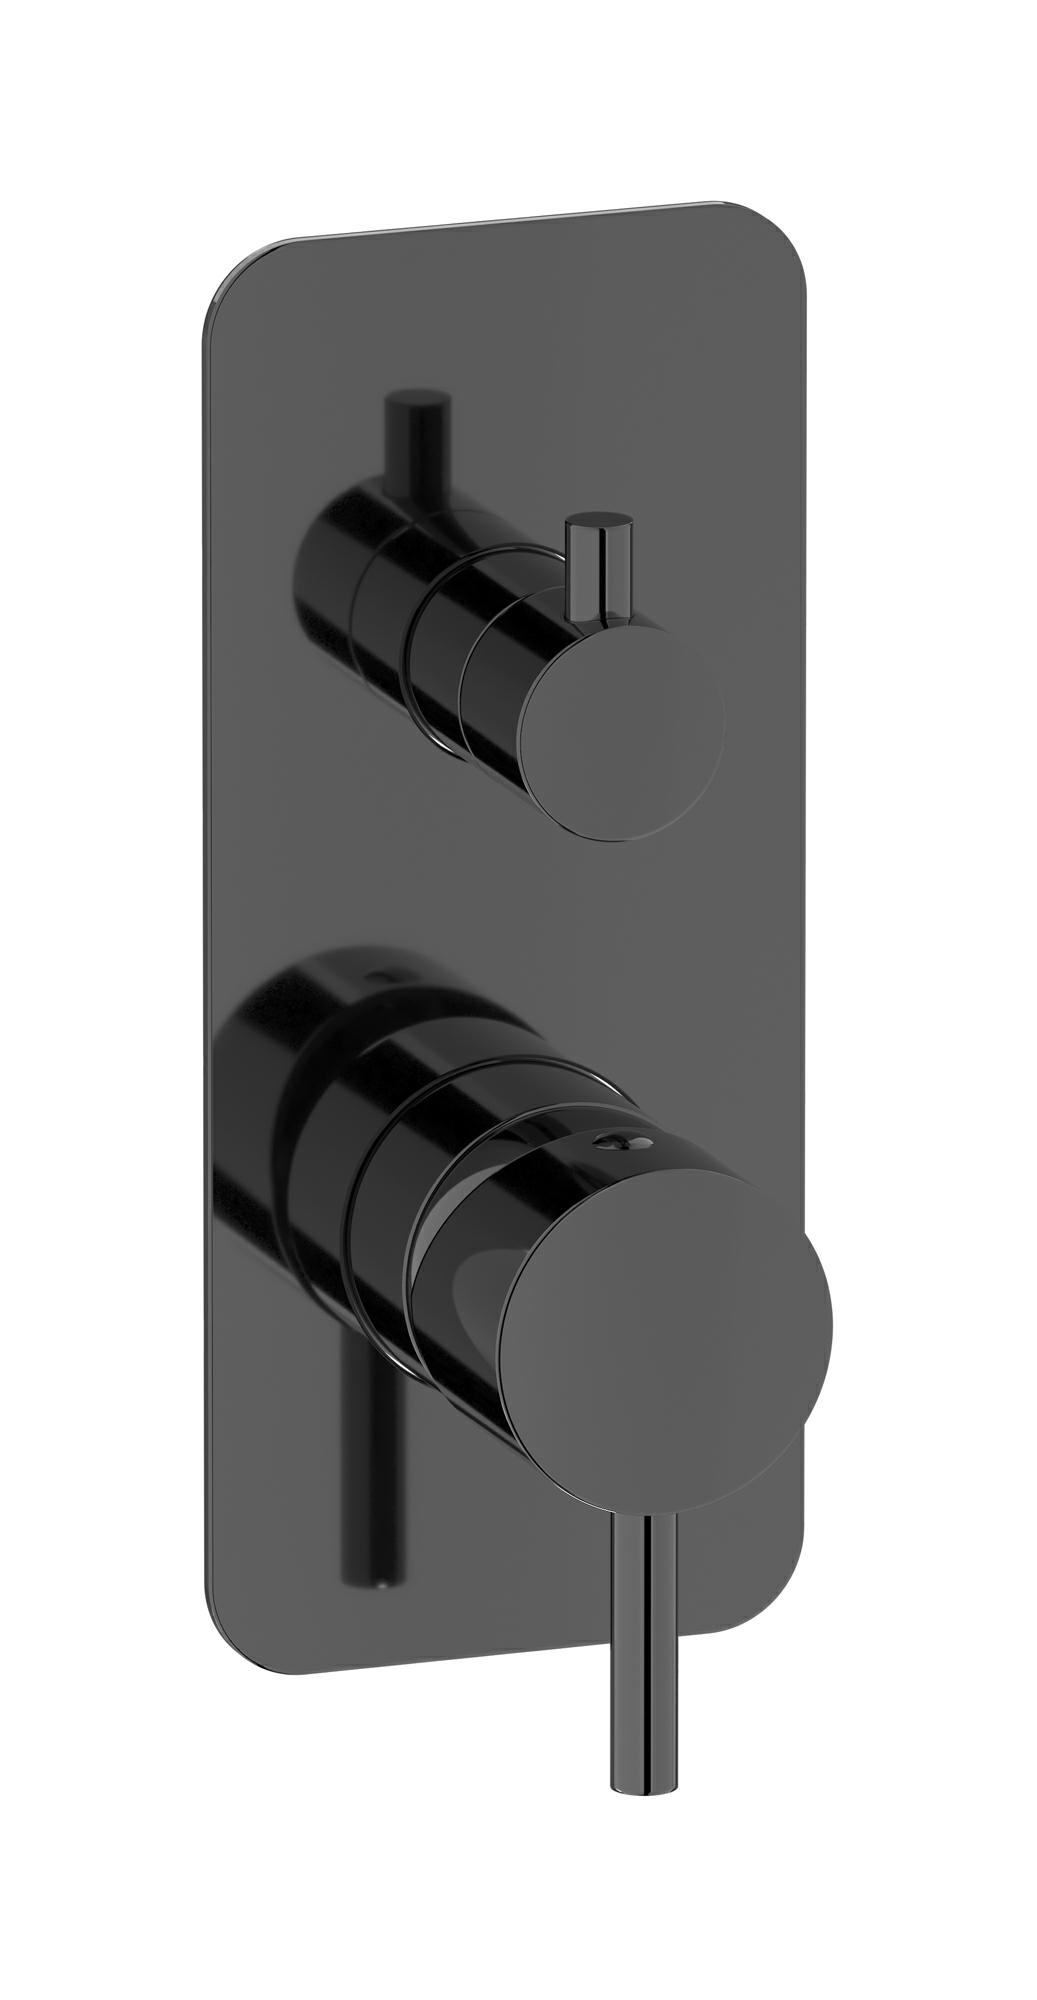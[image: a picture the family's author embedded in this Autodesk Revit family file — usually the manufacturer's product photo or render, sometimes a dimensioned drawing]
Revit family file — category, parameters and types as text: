
# Revit family: MT312
name_source: partatom
category: Apparecchi idraulici
units: mm (PartAtom-declared; Revit-internal decimal feet)

## family parameters
Basato su piano di lavoro = No
Condiviso = No
Mantieni orientamento annotazione = No
Numero OmniClass = 23.45.55.17
Punto di calcolo locali = No
Quota connettore circolare = Usa diametro
Sempre verticale = Sì
Taglio con vuoti quando caricato = No
Tipo di parte = Normale
Titolo OmniClass = Mixing Faucets

## types (13) — shared parameters
Cold water inlet = 10 mm  [stored 0.0328084 ft]
Commenti sul tipo = Wall mixer
Connessione CW = No
Connessione HW = No
Connessione di scarico = No
Connessione di ventilazione = No
Descrizione = Exposed parts for manual wall mixer with three ways diverter
Hot water inlet = 10 mm  [stored 0.0328084 ft]
Produttore = IB Rubinetterie S.p.A.
URL = https://www.weareib.it
zero-valued in all types: Prospetto di default

## per-type parameters (varying)
| type | Finishes surface | Immagine tipo | Modello |
| Chrome | IB_Chrome | MT312CC.jpg | MT312CC |
| Brushed nickel | IB_Brushed nickel | MT312SS.jpg | MT312SS |
| Matt white | IB_matt white | MT312BO.jpg | MT312BO |
| Matt black | IB_matt black | MT312NP.jpg | MT312NP |
| Natural brass | IB_Brass | MT312ON.jpg | MT312ON |
| Black chrome | IB_Black chrome | MT312CF.jpg | MT312CF |
| Brushed black chrome | IB_Brushed black chrome | MT312CS.jpg | MT312CS |
| Pale gold | IB_Pale gold | MT312II.jpg | MT312II |
| Brushed pale gold | IB_brushed pale gold | MT312IS.jpg | MT312IS |
| Rose gold | IB_Rose gold | MT312RS.jpg | MT312RS |
| Brushed rose gold | IB_Brushed rose gold | MT312SR.jpg | MT312SR |
| Gold | IB_gold | MT312OO.jpg | MT312OO |
| Brushed gold | IB_brushed gold | MT312OS.jpg | MT312OS |

note: [stored X ft] marks values corroborated as IEEE doubles in the binary element streams (Revit-internal decimal feet)
